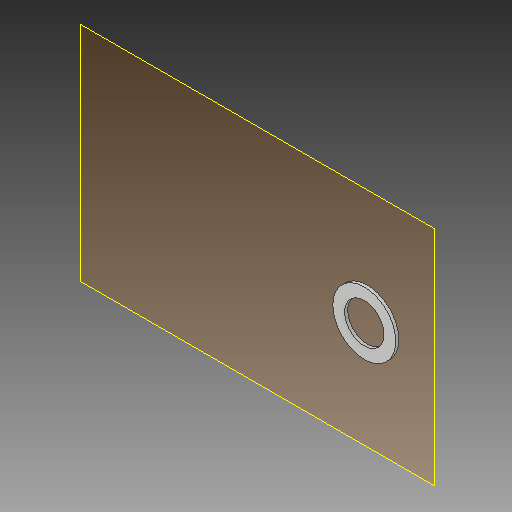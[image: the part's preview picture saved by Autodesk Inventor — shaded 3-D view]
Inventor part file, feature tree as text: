
AUTODESK INVENTOR PART (.ipt)
format: ipt  version: 2018 (Build 220112000, 112)  size: 89,088 bytes
history: native  units: mm
features: other x3, plane x1, extrude x1, sketch x1, reference x1
ambient origin geometry x8: Origin, YZ Plane, XZ Plane, XY Plane, X Axis, Y Axis, Z Axis, Center Point
bodies: Solid1 (feature_tree)
feature tree (7):
  plane  "Work Plane1"
  extrude  "Extrusion1"  [1 undecoded]
  sketch  "Sketch1"  dims[d0=0.5mm d1=0.0mm]
  reference  "Reference1"
  other  "<userpath>\OneDrive\SL-Inventor\SL-Beast 3D Printer\x-aXIS-aSSEMBLY.iam"
  other  "x-aXIS-aSSEMBLY.iam"
  other  "X-Idler:1"
note: 1 required parameter value undecoded (feature->parameter linkage not recoverable at this tier; creation-order binding heuristic only, values carry confidence <= 0.55)
